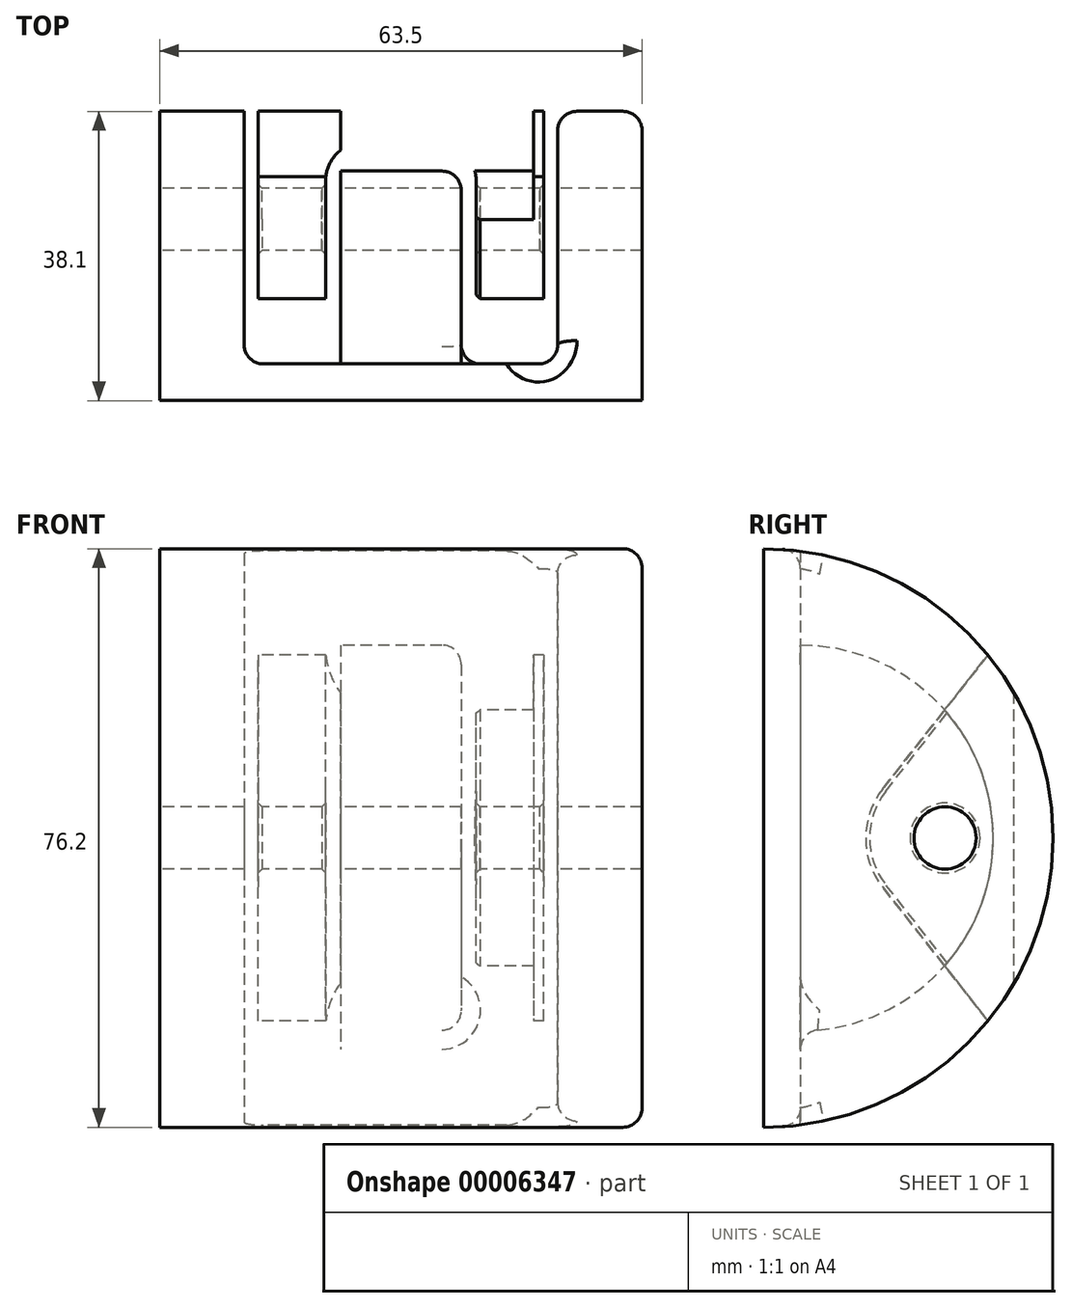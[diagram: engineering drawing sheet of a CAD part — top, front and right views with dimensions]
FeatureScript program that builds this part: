
annotation { "Feature Type Name" : "Feature", "Feature Type Description" : "" }
export const myFeature = defineFeature(function(context is Context, id is Id, definition is map)
    precondition{}
    {
        {
            var Q0;
            Q0=qCreatedBy(makeId("Right.planeOp"),FACE);
            var sketch = newSketch(context, id + "F0", { "sketchPlane" : qUnion([Q0])});
            skCircle(sketch, "E0", {"center": v(0, 0) * mm, "radius": 4.1 * mm});
            skArc(sketch, "E1", {"start": v(-8.21, 6.45) * mm, "mid": v(-10.45, 0) * mm, "end": v(-8.21, -6.45) * mm});
            skLineSegment(sketch, "E2.bottom", {"start": v(12.63, 29.85) * mm, "end": v(48.26, 29.85) * mm});
            skLineSegment(sketch, "E2.top", {"start": v(12.63, -29.84) * mm, "end": v(48.26, -29.84) * mm});
            skLineSegment(sketch, "E2.left", {"start": v(10.16, 29.85) * mm, "end": v(10.16, -29.84) * mm, "construction": true});
            skLineSegment(sketch, "E2.right", {"start": v(48.26, 29.85) * mm, "end": v(48.26, 18.42) * mm});
            skLineSegment(sketch, "E3", {"start": v(48.26, -29.84) * mm, "end": v(10.16, 29.85) * mm, "construction": true});
            skLineSegment(sketch, "E4", {"start": v(8.63, 27.9) * mm, "end": v(-8.21, 6.45) * mm});
            skLineSegment(sketch, "E5", {"start": v(8.63, -27.9) * mm, "end": v(-8.21, -6.45) * mm});
            skLineSegment(sketch, "E6", {"start": v(48.26, 18.42) * mm, "end": v(21.6, 18.42) * mm});
            skLineSegment(sketch, "E7", {"start": v(16.51, 13.34) * mm, "end": v(16.51, -13.34) * mm});
            skLineSegment(sketch, "E8", {"start": v(21.6, -18.42) * mm, "end": v(48.26, -18.42) * mm});
            skLineSegment(sketch, "E9", {"start": v(16.51, 18.42) * mm, "end": v(48.26, -18.41) * mm, "construction": true});
            skPoint(sketch, "E10", {"position": v(32.38, 0) * mm});
            skPoint(sketch, "E11", {"position": v(29.21, 0) * mm});
            skLineSegment(sketch, "E12.trimOffspring", {"start": v(48.26, -18.42) * mm, "end": v(48.26, -29.84) * mm});
            skPoint(sketch, "E13.visualSharp", {"position": v(16.5, -18.42) * mm});
            skArc(sketch, "E13.filletArc", {"start": v(16.51, -13.34) * mm, "mid": v(18, -16.93) * mm, "end": v(21.6, -18.42) * mm});
            skPoint(sketch, "E14.visualSharp", {"position": v(16.51, 18.42) * mm});
            skArc(sketch, "E14.filletArc", {"start": v(21.6, 18.42) * mm, "mid": v(18, 16.93) * mm, "end": v(16.51, 13.34) * mm});
            skPoint(sketch, "E15.visualSharp", {"position": v(10.16, -29.84) * mm});
            skArc(sketch, "E15.filletArc", {"start": v(8.63, -27.9) * mm, "mid": v(10.4, -29.33) * mm, "end": v(12.63, -29.84) * mm});
            skPoint(sketch, "E16.visualSharp", {"position": v(10.16, 29.85) * mm});
            skArc(sketch, "E16.filletArc", {"start": v(12.63, 29.85) * mm, "mid": v(10.4, 29.33) * mm, "end": v(8.63, 27.9) * mm});
            skSolve(sketch);
        }
        {
            var Q0;
            Q0 = qSketchRegion(id + "F0", true);
            extrude(context, id + "F1", {"entities" : qUnion([Q0]), "flatOperationType" : FlatOperationType.REMOVE, "depth" : 37.6 * mm, "offsetDistance" : 25.4 * mm, "domain" : OperationDomain.MODEL});
        }
        {
            var Q0;
            Q0=qCreatedBy(makeId("Top.planeOp"),FACE);
            var sketch = newSketch(context, id + "F2", { "sketchPlane" : qUnion([Q0])});
            skCircle(sketch, "E17", {"center": v(18.8, 29.21) * mm, "radius": 6.48 * mm});
            skLineSegment(sketch, "E18", {"start": v(37.13, 17.65) * mm, "end": v(30.58, 33.95) * mm});
            skLineSegment(sketch, "E19", {"start": v(0.46, 17.65) * mm, "end": v(7.01, 33.95) * mm});
            skLineSegment(sketch, "E20.bottom", {"start": v(0, 16.51) * mm, "end": v(37.6, 16.51) * mm, "construction": true});
            skLineSegment(sketch, "E20.top", {"start": v(0, -15.87) * mm, "end": v(8.9, -15.87) * mm});
            skLineSegment(sketch, "E20.left", {"start": v(0, 15.28) * mm, "end": v(0, -15.88) * mm});
            skLineSegment(sketch, "E20.right", {"start": v(37.6, 15.28) * mm, "end": v(37.6, -15.87) * mm});
            skLineSegment(sketch, "E21", {"start": v(28.7, -15.87) * mm, "end": v(28.7, 5.08) * mm});
            skLineSegment(sketch, "E22", {"start": v(23.62, 10.16) * mm, "end": v(13.97, 10.16) * mm});
            skLineSegment(sketch, "E23", {"start": v(8.9, 5.08) * mm, "end": v(8.9, -15.87) * mm});
            skLineSegment(sketch, "E24", {"start": v(28.7, -15.87) * mm, "end": v(8.89, 10.16) * mm, "construction": true});
            skPoint(sketch, "E25", {"position": v(18.8, -2.86) * mm});
            skLineSegment(sketch, "E26", {"start": v(18.8, -2.86) * mm, "end": v(18.8, 55.85) * mm, "construction": true});
            skLineSegment(sketch, "E27.trimOffspring", {"start": v(28.7, -15.87) * mm, "end": v(37.6, -15.87) * mm});
            skArc(sketch, "E28.trimOffspring", {"start": v(30.58, 33.95) * mm, "mid": v(18.8, 41.91) * mm, "end": v(7.01, 33.95) * mm});
            skPoint(sketch, "E29.visualSharp", {"position": v(8.89, 10.16) * mm});
            skArc(sketch, "E29.filletArc", {"start": v(13.97, 10.16) * mm, "mid": v(10.38, 8.67) * mm, "end": v(8.9, 5.08) * mm});
            skPoint(sketch, "E30.visualSharp", {"position": v(28.7, 10.16) * mm});
            skArc(sketch, "E30.filletArc", {"start": v(28.7, 5.08) * mm, "mid": v(27.21, 8.67) * mm, "end": v(23.62, 10.16) * mm});
            skPoint(sketch, "E31.visualSharp", {"position": v(0, 16.51) * mm});
            skArc(sketch, "E31.filletArc", {"start": v(0.46, 17.65) * mm, "mid": v(0.12, 16.49) * mm, "end": v(0, 15.28) * mm});
            skPoint(sketch, "E32.visualSharp", {"position": v(37.6, 16.51) * mm});
            skArc(sketch, "E32.filletArc", {"start": v(37.6, 15.28) * mm, "mid": v(37.48, 16.49) * mm, "end": v(37.13, 17.65) * mm});
            skSolve(sketch);
        }
        {
            var Q0;
            Q0 = qSketchRegion(id + "F2", true);
            extrude(context, id + "F3", {"entities" : qUnion([Q0]), "operationType" : NewBodyOperationType.INTERSECT, "oppositeDirection" : true, "depth" : 76.2 * mm, "symmetric" : true});
        }
        {
            var Q0;
            Q0=qCreatedBy(makeId("Top.planeOp"),FACE);
            var sketch = newSketch(context, id + "F4", { "sketchPlane" : qUnion([Q0])});
            skLineSegment(sketch, "E33", {"start": v(50.55, -23.88) * mm, "end": v(50.55, 14.22) * mm});
            skLineSegment(sketch, "E34", {"start": v(50.55, 14.22) * mm, "end": v(39.43, 14.22) * mm});
            skLineSegment(sketch, "E35", {"start": v(39.43, 14.22) * mm, "end": v(39.43, -19.05) * mm});
            skLineSegment(sketch, "E36", {"start": v(39.43, -19.05) * mm, "end": v(26.73, -19.05) * mm});
            skLineSegment(sketch, "E37", {"start": v(26.73, -19.05) * mm, "end": v(26.73, 6.35) * mm});
            skLineSegment(sketch, "E38", {"start": v(26.73, 6.35) * mm, "end": v(10.86, 6.35) * mm});
            skLineSegment(sketch, "E39", {"start": v(10.86, 6.35) * mm, "end": v(10.86, -19.05) * mm});
            skLineSegment(sketch, "E40", {"start": v(10.86, -19.05) * mm, "end": v(-1.84, -19.05) * mm});
            skLineSegment(sketch, "E41", {"start": v(-1.84, -19.05) * mm, "end": v(-1.84, 14.22) * mm});
            skLineSegment(sketch, "E42", {"start": v(-1.84, 14.22) * mm, "end": v(-12.95, 14.22) * mm});
            skLineSegment(sketch, "E43", {"start": v(-12.95, 14.22) * mm, "end": v(-12.95, -23.88) * mm});
            skLineSegment(sketch, "E44", {"start": v(-12.95, -23.88) * mm, "end": v(50.55, -23.88) * mm});
            skPoint(sketch, "E45", {"position": v(18.8, 6.35) * mm});
            skPoint(sketch, "E46", {"position": v(18.8, -23.88) * mm});
            skPoint(sketch, "E47", {"position": v(10.86, -6.35) * mm});
            skPoint(sketch, "E48", {"position": v(26.73, -6.35) * mm});
            skSolve(sketch);
        }
        {
            var Q0;
            Q0 = qSketchRegion(id + "F4", true);
            extrude(context, id + "F5", {"entities" : qUnion([Q0]), "depth" : 76.2 * mm, "symmetric" : true});
        }
        {
            var Q0;
            Q0=makeQuery(id+"F5.opExtrude","SWEPT_FACE",FACE,{"disambiguationData":[OSD([sQuery(id+"F4.wireOp",EDGE,"E43")])]});
            var sketch = newSketch(context, id + "F6", { "sketchPlane" : qUnion([Q0])});
            skArc(sketch, "E49", {"start": v(23.88, 38.1) * mm, "mid": v(-14.22, 0) * mm, "end": v(23.88, -38.1) * mm});
            skCircle(sketch, "E50", {"center": v(0, 0) * mm, "radius": 4.1 * mm});
            skLineSegment(sketch, "E51", {"start": v(23.88, -38.1) * mm, "end": v(23.88, 38.1) * mm});
            skSolve(sketch);
        }
        {
            var Q0;
            Q0 = qSketchRegion(id + "F6", true);
            extrude(context, id + "F7", {"entities" : qUnion([Q0]), "operationType" : NewBodyOperationType.INTERSECT, "endBound" : BoundingType.THROUGH_ALL, "oppositeDirection" : true, "depth" : 25.4 * mm});
        }
        {
            var Q0;
            Q0=makeQuery(id+"F5.opExtrude","SWEPT_FACE",FACE,{"disambiguationData":[OSD([sQuery(id+"F4.wireOp",EDGE,"E39")])]});
            var sketch = newSketch(context, id + "F8", { "sketchPlane" : qUnion([Q0])});
            skLineSegment(sketch, "E52", {"start": v(19.05, 37.8) * mm, "end": v(19.05, 25.4) * mm});
            skLineSegment(sketch, "E53", {"start": v(19.05, 37.8) * mm, "end": v(-17.02, 33.19) * mm});
            skLineSegment(sketch, "E54", {"start": v(19.05, -37.8) * mm, "end": v(19.05, -25.4) * mm});
            skLineSegment(sketch, "E55", {"start": v(19.05, -37.8) * mm, "end": v(-32.86, -31.16) * mm});
            skArc(sketch, "E56", {"start": v(19.05, 25.4) * mm, "mid": v(-6.35, 0) * mm, "end": v(19.05, -25.4) * mm});
            skLineSegment(sketch, "E57", {"start": v(-17.02, 33.19) * mm, "end": v(-32.86, -31.16) * mm});
            skSolve(sketch);
        }
        {
            var Q0;
            Q0 = qSketchRegion(id + "F8", true);
            extrude(context, id + "F9", {"entities" : qUnion([Q0]), "operationType" : NewBodyOperationType.REMOVE, "oppositeDirection" : true, "depth" : 25.4 * mm});
        }
        {
            var Q0;
            Q0=makeQuery(id+"F5.opExtrude","SWEPT_EDGE",EDGE,{"disambiguationData":[OSD([sQuery(id+"F4.wireOp",EDGE,"E35"),sQuery(id+"F4.wireOp",EDGE,"E36")])]});
            var Q1;
            Q1=makeQuery(id+"F5.opExtrude","SWEPT_EDGE",EDGE,{"disambiguationData":[OSD([sQuery(id+"F4.wireOp",EDGE,"E40"),sQuery(id+"F4.wireOp",EDGE,"E41")])]});
            var Q2;
            Q2=makeQuery(id+"F9.boolean.opBoolean","INTERSECT",EDGE,{"derivedFrom":[makeQuery(id+"F5.opExtrude","SWEPT_FACE",FACE,{"disambiguationData":[OSD([sQuery(id+"F4.wireOp",EDGE,"E37")])]}),makeQuery(id+"F9.opExtrude","SWEPT_FACE",FACE,{"disambiguationData":[OSD([sQuery(id+"F8.wireOp",EDGE,"E56")])]})]});
            var Q3;
            Q3=makeQuery(id+"F9.boolean.opBoolean","COPY",EDGE,{"derivedFrom":makeQuery(id+"F9.opExtrude","CAP_EDGE",EDGE,{"disambiguationData":[OSD([sQuery(id+"F8.wireOp",EDGE,"E56")])],"isStart":true})});
            var Q4;
            Q4=makeQuery(id+"F9.boolean.opBoolean","COPY",EDGE,{"derivedFrom":makeQuery(id+"F9.opExtrude","SWEPT_EDGE",EDGE,{"disambiguationData":[OSD([sQuery(id+"F4.wireOp",EDGE,"E39"),sQuery(id+"F4.wireOp",EDGE,"E40"),sQuery(id+"F8.wireOp",EDGE,"E54"),sQuery(id+"F8.wireOp",EDGE,"E56")])]})});
            var Q5;
            Q5=makeQuery(id+"F7.boolean.opBoolean","INTERSECT",EDGE,{"derivedFrom":[makeQuery(id+"F5.opExtrude","SWEPT_FACE",FACE,{"disambiguationData":[OSD([sQuery(id+"F4.wireOp",EDGE,"E35")])]}),makeQuery(id+"F7.opExtrude","SWEPT_FACE",FACE,{"disambiguationData":[OSD([sQuery(id+"F6.wireOp",EDGE,"E49")])]})]});
            var Q6;
            Q6=makeQuery(id+"F7.boolean.opBoolean","INTERSECT",EDGE,{"derivedFrom":[makeQuery(id+"F5.opExtrude","SWEPT_FACE",FACE,{"disambiguationData":[OSD([sQuery(id+"F4.wireOp",EDGE,"E33")])]}),makeQuery(id+"F7.opExtrude","SWEPT_FACE",FACE,{"disambiguationData":[OSD([sQuery(id+"F6.wireOp",EDGE,"E49")])]})]});
            var Q7;
            Q7=makeQuery(id+"F7.boolean.opBoolean","COPY",EDGE,{"derivedFrom":makeQuery(id+"F7.opExtrude","CAP_EDGE",EDGE,{"disambiguationData":[OSD([sQuery(id+"F6.wireOp",EDGE,"E49")])],"isStart":true})});
            fillet(context, id + "F10", {"entities" : qUnion([Q0, Q1, Q2, Q3, Q4, Q5, Q6, Q7]), "radius" : 2.54 * mm, "tangentPropagation" : true, "allowEdgeOverflow" : false});
        }
        {
            var Q0;
            Q0=makeQuery(id+"F3.boolean.opBoolean","INTERSECT",EDGE,{"derivedFrom":[makeQuery(id+"F1.opExtrude","SWEPT_FACE",FACE,{"disambiguationData":[OSD([sQuery(id+"F0.wireOp",EDGE,"E2.bottom")])]}),makeQuery(id+"F3.opExtrude","SWEPT_FACE",FACE,{"disambiguationData":[OSD([sQuery(id+"F2.wireOp",EDGE,"E17")])]})]});
            var Q1;
            Q1=makeQuery(id+"F3.boolean.opBoolean","INTERSECT",EDGE,{"derivedFrom":[makeQuery(id+"F1.opExtrude","SWEPT_FACE",FACE,{"disambiguationData":[OSD([sQuery(id+"F0.wireOp",EDGE,"E2.top")])]}),makeQuery(id+"F3.opExtrude","SWEPT_FACE",FACE,{"disambiguationData":[OSD([sQuery(id+"F2.wireOp",EDGE,"E17")])]})]});
            var Q2;
            Q2=makeQuery(id+"F1.opExtrude","CAP_EDGE",EDGE,{"disambiguationData":[OSD([sQuery(id+"F0.wireOp",EDGE,"E0")])],"isStart":true});
            var Q3;
            Q3=makeQuery(id+"F1.opExtrude","CAP_EDGE",EDGE,{"disambiguationData":[OSD([sQuery(id+"F0.wireOp",EDGE,"E0")])],"isStart":false});
            var Q4;
            Q4=makeQuery(id+"F3.boolean.opBoolean","INTERSECT",EDGE,{"derivedFrom":[makeQuery(id+"F1.opExtrude","SWEPT_FACE",FACE,{"disambiguationData":[OSD([sQuery(id+"F0.wireOp",EDGE,"E8")])]}),makeQuery(id+"F3.opExtrude","SWEPT_FACE",FACE,{"disambiguationData":[OSD([sQuery(id+"F2.wireOp",EDGE,"E17")])]})]});
            var Q5;
            Q5=makeQuery(id+"F3.boolean.opBoolean","INTERSECT",EDGE,{"derivedFrom":[makeQuery(id+"F1.opExtrude","SWEPT_FACE",FACE,{"disambiguationData":[OSD([sQuery(id+"F0.wireOp",EDGE,"E6")])]}),makeQuery(id+"F3.opExtrude","SWEPT_FACE",FACE,{"disambiguationData":[OSD([sQuery(id+"F2.wireOp",EDGE,"E17")])]})]});
            var Q6;
            Q6=makeQuery(id+"F3.boolean.opBoolean","INTERSECT",EDGE,{"derivedFrom":[makeQuery(id+"F1.opExtrude","SWEPT_FACE",FACE,{"disambiguationData":[OSD([sQuery(id+"F0.wireOp",EDGE,"E0")])]}),makeQuery(id+"F3.opExtrude","SWEPT_FACE",FACE,{"disambiguationData":[OSD([sQuery(id+"F2.wireOp",EDGE,"E21")])]})]});
            var Q7;
            Q7=makeQuery(id+"F3.boolean.opBoolean","INTERSECT",EDGE,{"derivedFrom":[makeQuery(id+"F1.opExtrude","SWEPT_FACE",FACE,{"disambiguationData":[OSD([sQuery(id+"F0.wireOp",EDGE,"E0")])]}),makeQuery(id+"F3.opExtrude","SWEPT_FACE",FACE,{"disambiguationData":[OSD([sQuery(id+"F2.wireOp",EDGE,"E23")])]})]});
            chamfer(context, id + "F11", {"entities" : qUnion([Q0, Q1, Q2, Q3, Q4, Q5, Q6, Q7]), "width" : 0.5 * mm, "tangentPropagation" : true});
        }
        {
            var Q0;
            Q0=makeQuery(id+"F3.boolean.opBoolean","INTERSECT",EDGE,{"derivedFrom":[makeQuery(id+"F1.opExtrude","SWEPT_FACE",FACE,{"disambiguationData":[OSD([sQuery(id+"F0.wireOp",EDGE,"E6")])]}),makeQuery(id+"F3.opExtrude","SWEPT_FACE",FACE,{"disambiguationData":[OSD([sQuery(id+"F2.wireOp",EDGE,"E28.trimOffspring")])]})]});
            var Q1;
            Q1=makeQuery(id+"F3.boolean.opBoolean","INTERSECT",EDGE,{"derivedFrom":[makeQuery(id+"F1.opExtrude","SWEPT_FACE",FACE,{"disambiguationData":[OSD([sQuery(id+"F0.wireOp",EDGE,"E2.bottom")])]}),makeQuery(id+"F3.opExtrude","SWEPT_FACE",FACE,{"disambiguationData":[OSD([sQuery(id+"F2.wireOp",EDGE,"E18")])]})]});
            var Q2;
            Q2=makeQuery(id+"F3.boolean.opBoolean","INTERSECT",EDGE,{"derivedFrom":[makeQuery(id+"F1.opExtrude","SWEPT_FACE",FACE,{"disambiguationData":[OSD([sQuery(id+"F0.wireOp",EDGE,"E5")])]}),makeQuery(id+"F3.opExtrude","SWEPT_FACE",FACE,{"disambiguationData":[OSD([sQuery(id+"F2.wireOp",EDGE,"E21")])]})]});
            chamfer(context, id + "F12", {"entities" : qUnion([Q0, Q1, Q2]), "width" : 0.5 * mm, "tangentPropagation" : true});
        }
    });
